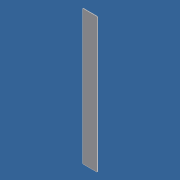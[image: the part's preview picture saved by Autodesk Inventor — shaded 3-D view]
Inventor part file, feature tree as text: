
AUTODESK INVENTOR PART (.ipt)
format: ipt  version: unknown  size: 168,960 bytes
history: native  units: in
note: dims shown in document units (in); Inventor stores cm internally (conversion verified against a paired STEP export)
features: extrude x1, fillet x1, sketch x1
ambient origin geometry x8: Origin, YZ Plane, XZ Plane, XY Plane, X Axis, Y Axis, Z Axis, Center Point
bodies: Solid1 (feature_tree)
feature tree (3):
  extrude  "Extrusion1"  Depth=37.0in
  fillet  "Fillet1"  Radius=0.125in
  sketch  "Sketch1"  dims[d0=4.0in d1=37.0in d2=0.125in d3=0.0in d4=0.125in]
